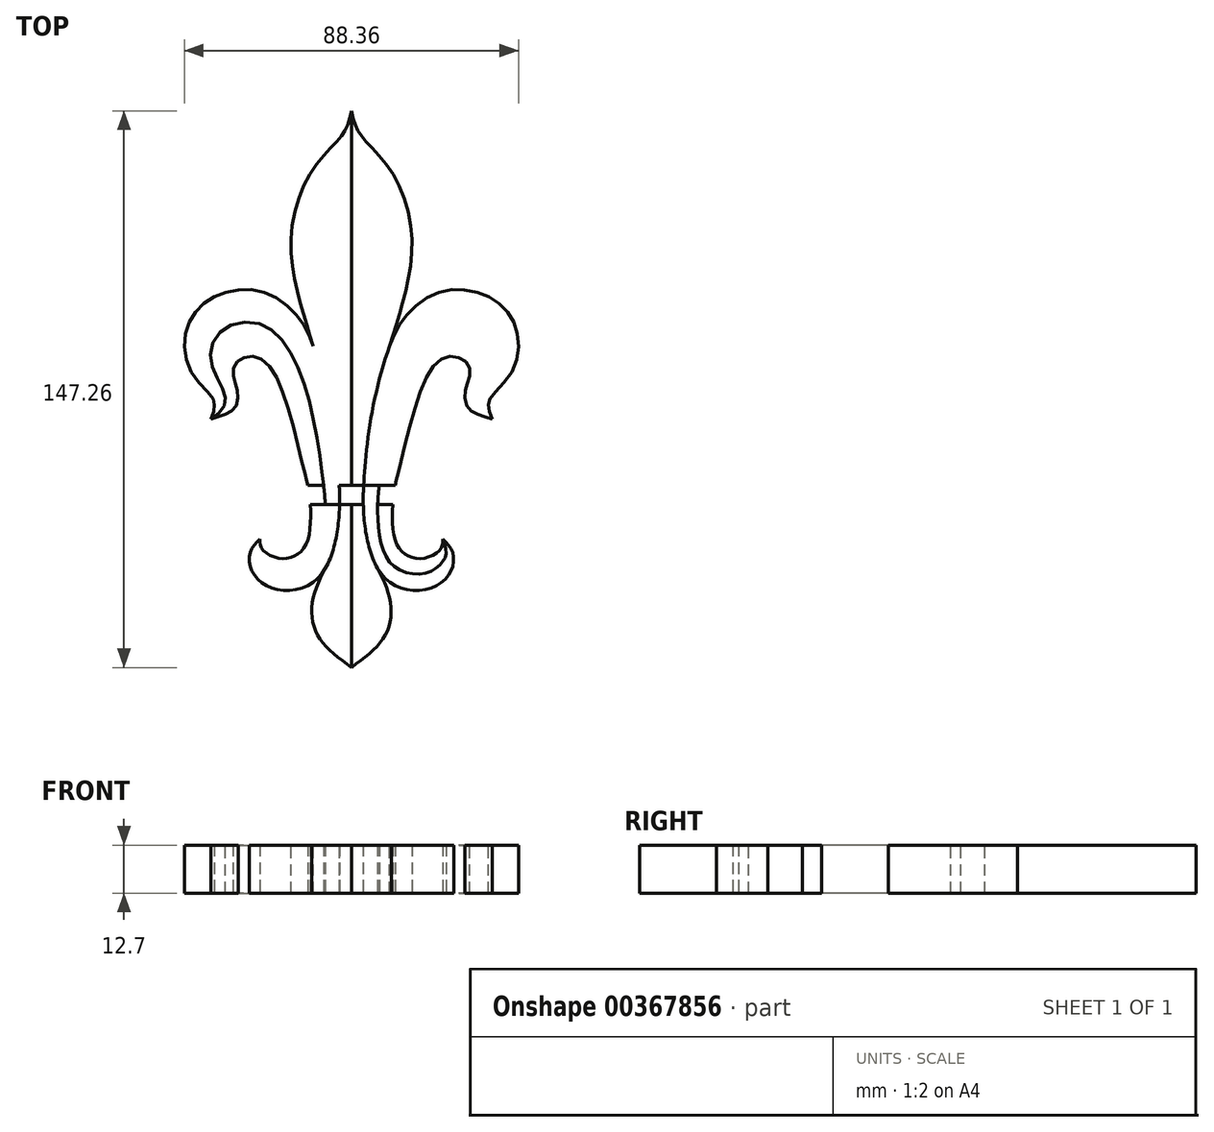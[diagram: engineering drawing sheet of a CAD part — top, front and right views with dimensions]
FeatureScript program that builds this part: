
annotation { "Feature Type Name" : "Feature", "Feature Type Description" : "" }
export const myFeature = defineFeature(function(context is Context, id is Id, definition is map)
    precondition{}
    {
        {
            var Q0;
            Q0=qCreatedBy(makeId("Top.planeOp"),FACE);
            var sketch = newSketch(context, id + "F0", { "sketchPlane" : qUnion([Q0])});
            skLineSegment(sketch, "E0", {"start": v(0, 2.54) * mm, "end": v(0, 101.6) * mm});
            skFitSpline(sketch, "E1", {"points": [v(-10.1, 39.4) * mm, v(-4.9, 18.71) * mm, v(-3.3, 3.75) * mm, v(-3.18, -3.76) * mm, v(-5.19, -15.6) * mm, v(-11.1, -23.68) * mm, v(-20.33, -24.84) * mm, v(-26.07, -20.61) * mm, v(-26.8, -15.28) * mm, v(-24.22, -11.64) * mm], "startDerivative": vector(42.52, -120.3) * mm, "endDerivative": vector(40.28, 44.53) * mm});
            skFitSpline(sketch, "E2", {"points": [v(-10.1, 39.4) * mm, v(-13.94, 46.8) * mm, v(-22.2, 53.32) * mm, v(-32.15, 53.9) * mm, v(-40.14, 49.72) * mm, v(-44.02, 41.96) * mm, v(-42.08, 32.01) * mm, v(-36.74, 25.7) * mm, v(-36.26, 23.52) * mm, v(-37.2, 20.13) * mm], "startDerivative": vector(-26.96, 73.92) * mm, "endDerivative": vector(-24.3, -46.74) * mm});
            skFitSpline(sketch, "E3", {"points": [v(-37.2, 20.13) * mm, v(-33.59, 23.77) * mm, v(-34.07, 28.13) * mm, v(-37.2, 35.59) * mm, v(-34.46, 43.37) * mm, v(-24.22, 45.25) * mm, v(-15.71, 37.03) * mm, v(-10.1, 20.16) * mm, v(-7.48, 3.5) * mm, v(-6.92, -3.55) * mm, v(-8.07, -13.73) * mm, v(-12.2, -19.51) * mm, v(-19.17, -20.8) * mm, v(-23.53, -18.31) * mm, v(-25.07, -15.6) * mm, v(-24.22, -11.64) * mm], "startDerivative": vector(93.13, 59.89) * mm, "endDerivative": vector(26.35, 80.94) * mm});
            skFitSpline(sketch, "E4", {"points": [v(-37.2, 20.13) * mm, v(-33.59, 21.31) * mm, v(-30.86, 23.01) * mm, v(-30, 26.79) * mm, v(-30.95, 30.3) * mm, v(-31.03, 34.16) * mm, v(-27.69, 36.56) * mm, v(-22.63, 35.1) * mm, v(-16.28, 21.31) * mm, v(-12.17, 5) * mm, v(-11.67, 3.01) * mm, v(-10.86, -3.13) * mm, v(-11.82, -12.66) * mm, v(-15.08, -16.17) * mm, v(-19.75, -16.62) * mm, v(-23.74, -14.11) * mm, v(-24.22, -11.64) * mm], "startDerivative": vector(76.44, 20.6) * mm, "endDerivative": vector(-2.62, 61.96) * mm});
            skFitSpline(sketch, "E5", {"points": [v(-10.1, 39.4) * mm, v(-13.7, 51.45) * mm, v(-16, 67.45) * mm, v(-11.14, 84.61) * mm, v(-4.03, 93.41) * mm, v(-1.44, 97.02) * mm, v(0, 101.6) * mm], "startDerivative": vector(-20.19, 63.74) * mm, "endDerivative": vector(10.85, 43.29) * mm});
            skFitSpline(sketch, "E6", {"points": [v(-6.92, -19.4) * mm, v(-10.1, -27.14) * mm, v(-10.1, -34.2) * mm, v(-6.92, -39.83) * mm, v(0, -45.66) * mm], "startDerivative": vector(-14.7, -29.44) * mm, "endDerivative": vector(28.09, -21) * mm});
            skLineSegment(sketch, "E7", {"start": v(0, -2.54) * mm, "end": v(0, -45.66) * mm});
            skArc(sketch, "E8", {"start": v(-13.66, -2.54) * mm, "mid": v(-16.2, 0) * mm, "end": v(-13.66, 2.54) * mm});
            skFitSpline(sketch, "E9.MirrorCS", {"points": [v(6.92, -19.4) * mm, v(10.1, -27.14) * mm, v(10.1, -34.2) * mm, v(6.92, -39.83) * mm, v(0, -45.66) * mm], "startDerivative": vector(14.7, -29.44) * mm, "endDerivative": vector(-28.09, -21) * mm});
            skFitSpline(sketch, "E10.MirrorCS", {"points": [v(37.2, 20.13) * mm, v(33.59, 21.31) * mm, v(30.86, 23.01) * mm, v(30, 26.79) * mm, v(30.95, 30.3) * mm, v(31.03, 34.16) * mm, v(27.69, 36.56) * mm, v(22.63, 35.1) * mm, v(16.28, 21.31) * mm, v(12.17, 5) * mm, v(11.67, 3.01) * mm, v(10.86, -3.13) * mm, v(11.82, -12.66) * mm, v(15.08, -16.17) * mm, v(19.75, -16.62) * mm, v(23.74, -14.11) * mm, v(24.22, -11.64) * mm], "startDerivative": vector(-76.44, 20.6) * mm, "endDerivative": vector(2.62, 61.96) * mm});
            skFitSpline(sketch, "E11.MirrorCS", {"points": [v(10.1, 39.4) * mm, v(13.94, 46.8) * mm, v(22.2, 53.32) * mm, v(32.15, 53.9) * mm, v(40.14, 49.72) * mm, v(44.02, 41.96) * mm, v(42.08, 32.01) * mm, v(36.74, 25.7) * mm, v(36.26, 23.52) * mm, v(37.2, 20.13) * mm], "startDerivative": vector(26.96, 73.92) * mm, "endDerivative": vector(24.3, -46.74) * mm});
            skFitSpline(sketch, "E12.MirrorCS", {"points": [v(10.1, 39.4) * mm, v(4.9, 18.71) * mm, v(3.3, 3.75) * mm, v(3.18, -3.76) * mm, v(5.19, -15.6) * mm, v(11.1, -23.68) * mm, v(20.33, -24.84) * mm, v(26.07, -20.61) * mm, v(26.8, -15.28) * mm, v(24.22, -11.64) * mm], "startDerivative": vector(-42.52, -120.3) * mm, "endDerivative": vector(-40.28, 44.53) * mm});
            skFitSpline(sketch, "E13.MirrorCS", {"points": [v(37.2, 20.13) * mm, v(33.59, 23.77) * mm, v(34.07, 28.13) * mm, v(37.2, 35.59) * mm, v(34.46, 43.37) * mm, v(24.22, 45.25) * mm, v(15.71, 37.03) * mm, v(10.1, 20.16) * mm, v(7.48, 3.5) * mm, v(6.92, -3.55) * mm, v(8.07, -13.73) * mm, v(12.2, -19.51) * mm, v(19.17, -20.8) * mm, v(23.53, -18.31) * mm, v(25.07, -15.6) * mm, v(24.22, -11.64) * mm], "startDerivative": vector(-93.13, 59.89) * mm, "endDerivative": vector(-26.35, 80.94) * mm});
            skArc(sketch, "E14.MirrorCS", {"start": v(13.66, -2.54) * mm, "mid": v(16.2, 0) * mm, "end": v(13.66, 2.54) * mm});
            skFitSpline(sketch, "E15.MirrorCS", {"points": [v(10.1, 39.4) * mm, v(13.7, 51.45) * mm, v(16, 67.45) * mm, v(11.14, 84.61) * mm, v(4.03, 93.41) * mm, v(1.44, 97.02) * mm, v(0, 101.6) * mm], "startDerivative": vector(20.19, 63.74) * mm, "endDerivative": vector(-10.85, 43.29) * mm});
            skLineSegment(sketch, "E16", {"start": v(-13.66, 2.54) * mm, "end": v(13.66, 2.54) * mm});
            skLineSegment(sketch, "E17", {"start": v(-13.66, -2.54) * mm, "end": v(13.66, -2.54) * mm});
            skFitSpline(sketch, "E18.trimOffspring", {"points": [v(-10.1, 39.4) * mm, v(-4.9, 18.71) * mm, v(-3.3, 3.75) * mm, v(-3.18, -3.76) * mm, v(-5.19, -15.6) * mm, v(-11.1, -23.68) * mm, v(-20.33, -24.84) * mm, v(-26.07, -20.61) * mm, v(-26.8, -15.28) * mm, v(-24.22, -11.64) * mm], "startDerivative": vector(42.52, -120.3) * mm, "endDerivative": vector(40.28, 44.53) * mm});
            skSolve(sketch);
        }
        {
            var Q0;
            {var subQ0=sQuery(id+"F0.wireOp",EDGE,"E0");Q0=makeQuery(id+"F0.imprint","IMPRINT",FACE,{"disambiguationData":[TD([[makeQuery(id+"F0.imprint","IMPRINT",EDGE,{"derivedFrom":subQ0}),1.0]])]});}
            var Q1;
            {var subQ0=sQuery(id+"F0.wireOp",EDGE,"E3");Q1=makeQuery(id+"F0.imprint","IMPRINT",FACE,{"disambiguationData":[TD([[makeQuery(id+"F0.imprint","IMPRINT",EDGE,{"derivedFrom":subQ0}),-1.0]])]});}
            var Q2;
            {var subQ0=sQuery(id+"F0.wireOp",EDGE,"E3");Q2=makeQuery(id+"F0.imprint","IMPRINT",FACE,{"disambiguationData":[TD([[makeQuery(id+"F0.imprint","IMPRINT",EDGE,{"derivedFrom":subQ0}),1.0]])]});}
            var Q3;
            {var subQ0=sQuery(id+"F0.wireOp",EDGE,"E6");Q3=makeQuery(id+"F0.imprint","IMPRINT",FACE,{"disambiguationData":[TD([[makeQuery(id+"F0.imprint","IMPRINT",EDGE,{"derivedFrom":subQ0}),1.0]])]});}
            var Q4;
            {var subQ3=sQuery(id+"F0.wireOp",EDGE,"E13.MirrorCS");Q4=makeQuery(id+"F0.imprint","IMPRINT",FACE,{"disambiguationData":[TD([[makeQuery(id+"F0.imprint","IMPRINT",EDGE,{"derivedFrom":subQ3}),-1.0]])]});}
            var Q5;
            {var subQ0=sQuery(id+"F0.wireOp",EDGE,"E10.MirrorCS");Q5=makeQuery(id+"F0.imprint","IMPRINT",FACE,{"disambiguationData":[TD([[makeQuery(id+"F0.imprint","IMPRINT",EDGE,{"derivedFrom":subQ0}),-1.0]])]});}
            var Q6;
            {var subQ8=sQuery(id+"F0.wireOp",EDGE,"E8");Q6=makeQuery(id+"F0.imprint","IMPRINT",FACE,{"disambiguationData":[TD([[makeQuery(id+"F0.imprint","IMPRINT",EDGE,{"derivedFrom":subQ8}),-1.0]])]});}
            extrude(context, id + "F1", {"entities" : qUnion([Q0, Q1, Q2, Q3, Q4, Q5, Q6]), "depth" : 12.7 * mm});
        }
        {
            var Q0;
            {var subQ0=sQuery(id+"F0.wireOp",EDGE,"E1");Q0=makeQuery(id+"F0.imprint","IMPRINT",FACE,{"disambiguationData":[TD([[makeQuery(id+"F0.imprint","IMPRINT",EDGE,{"derivedFrom":subQ0}),-1.0]])]});}
            var Q1;
            {var subQ0=sQuery(id+"F0.wireOp",EDGE,"E0");Q1=makeQuery(id+"F0.imprint","IMPRINT",FACE,{"disambiguationData":[TD([[makeQuery(id+"F0.imprint","IMPRINT",EDGE,{"derivedFrom":subQ0}),-1.0]])]});}
            var Q2;
            Q2=makeQuery(id+"F0.imprint","IMPRINT",FACE,{"disambiguationData":[TD([[makeQuery(id+"F0.imprint","IMPRINT",EDGE,{"derivedFrom":sQuery(id+"F0.wireOp",EDGE,"E11.MirrorCS")}),-1.0]])]});
            var Q3;
            {var subQ0=sQuery(id+"F0.wireOp",EDGE,"E4");Q3=makeQuery(id+"F0.imprint","IMPRINT",FACE,{"disambiguationData":[TD([[makeQuery(id+"F0.imprint","IMPRINT",EDGE,{"derivedFrom":subQ0}),1.0]])]});}
            var Q4;
            {var subQ0=sQuery(id+"F0.wireOp",EDGE,"E7");Q4=makeQuery(id+"F0.imprint","IMPRINT",FACE,{"disambiguationData":[TD([[makeQuery(id+"F0.imprint","IMPRINT",EDGE,{"derivedFrom":subQ0}),1.0]])]});}
            var Q5;
            {var subQ0=sQuery(id+"F0.wireOp",EDGE,"E13.MirrorCS");Q5=makeQuery(id+"F0.imprint","IMPRINT",FACE,{"disambiguationData":[TD([[makeQuery(id+"F0.imprint","IMPRINT",EDGE,{"derivedFrom":subQ0}),1.0]])]});}
            extrude(context, id + "F2", {"entities" : qUnion([Q0, Q1, Q2, Q3, Q4, Q5]), "depth" : 12.7 * mm});
        }
    });
